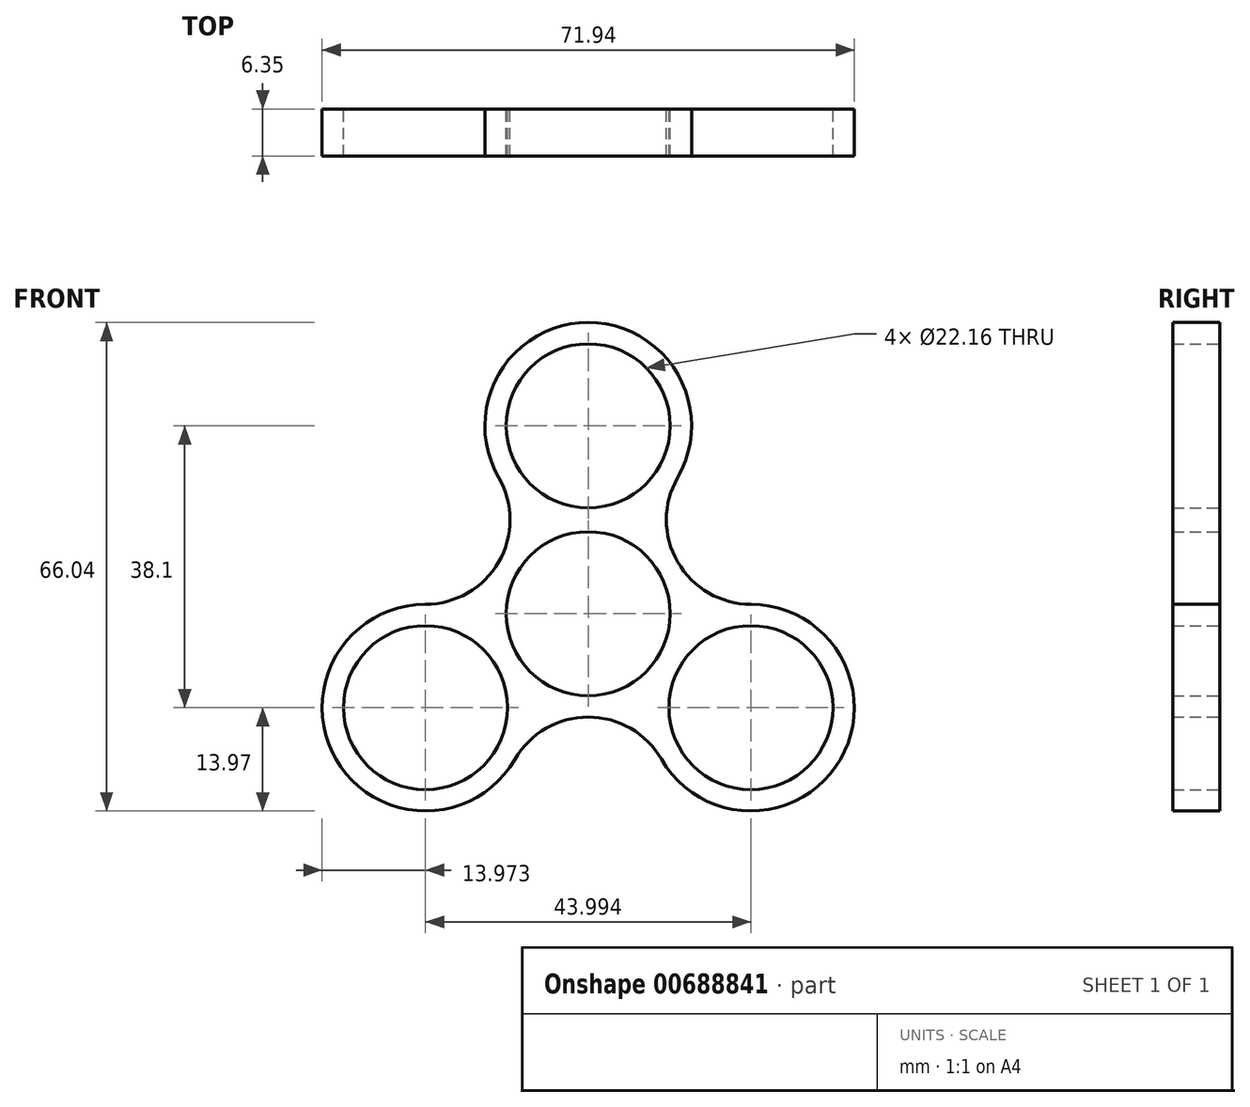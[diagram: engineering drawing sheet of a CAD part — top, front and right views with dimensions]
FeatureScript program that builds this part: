
annotation { "Feature Type Name" : "Feature", "Feature Type Description" : "" }
export const myFeature = defineFeature(function(context is Context, id is Id, definition is map)
    precondition{}
    {
        {
            var Q0;
            Q0=qCreatedBy(makeId("Front.planeOp"),FACE);
            var sketch = newSketch(context, id + "F0", { "sketchPlane" : qUnion([Q0])});
            skCircle(sketch, "E0", {"center": v(0, 0) * mm, "radius": 11.08 * mm});
            skLineSegment(sketch, "E1", {"start": v(0, 0) * mm, "end": v(0, 25.4) * mm});
            skCircle(sketch, "E2", {"center": v(0, 25.4) * mm, "radius": 11.08 * mm});
            skCircle(sketch, "E3.1.0", {"center": v(-22, -12.7) * mm, "radius": 11.08 * mm});
            skCircle(sketch, "E3.2.0", {"center": v(22, -12.7) * mm, "radius": 11.08 * mm});
            skCircle(sketch, "E4", {"center": v(0, 0) * mm, "radius": 13.97 * mm});
            skCircle(sketch, "E5", {"center": v(0, 25.4) * mm, "radius": 13.97 * mm});
            skCircle(sketch, "E6.1.0", {"center": v(-22, -12.7) * mm, "radius": 13.97 * mm});
            skCircle(sketch, "E6.2.0", {"center": v(22, -12.7) * mm, "radius": 13.97 * mm});
            skLineSegment(sketch, "E7", {"start": v(0, 0) * mm, "end": v(0, -25.4) * mm});
            skArc(sketch, "E8", {"start": v(9.9, -19.69) * mm, "mid": v(0, -13.97) * mm, "end": v(-9.9, -19.69) * mm});
            skArc(sketch, "E9.1.0", {"start": v(12.1, 18.41) * mm, "mid": v(12.1, 6.99) * mm, "end": v(22, 1.27) * mm});
            skArc(sketch, "E9.2.0", {"start": v(-22, 1.27) * mm, "mid": v(-12.1, 6.99) * mm, "end": v(-12.1, 18.42) * mm});
            skSolve(sketch);
        }
        {
            var Q0;
            {var subQ6=sQuery(id+"F0.wireOp",EDGE,"E1");var subQ7=sQuery(id+"F0.wireOp",EDGE,"E0");var subQ8=makeQuery(id+"F0.imprint","INTERSECT",VERTEX,{"derivedFrom":[subQ7,subQ6]});Q0=makeQuery(id+"F0.imprint","IMPRINT",FACE,{"disambiguationData":[TD([[makeQuery(id+"F0.imprint","IMPRINT",EDGE,{"disambiguationData":[TD([[subQ8,-1.0]])],"derivedFrom":subQ7}),-1.0]])]});}
            var Q1;
            {var subQ0=sQuery(id+"F0.wireOp",EDGE,"E6.1.0");var subQ1=sQuery(id+"F0.wireOp",EDGE,"E4");var subQ2=makeQuery(id+"F0.imprint","INTERSECT",VERTEX,{"disambiguationData":[OD(0.0)],"derivedFrom":[subQ1,subQ0]});Q1=makeQuery(id+"F0.imprint","IMPRINT",FACE,{"disambiguationData":[TD([[makeQuery(id+"F0.imprint","IMPRINT",EDGE,{"disambiguationData":[TD([[subQ2,-1.0]])],"derivedFrom":subQ1}),1.0]])]});}
            var Q2;
            Q2=makeQuery(id+"F0.imprint","IMPRINT",FACE,{"disambiguationData":[TD([[makeQuery(id+"F0.imprint","IMPRINT",EDGE,{"derivedFrom":sQuery(id+"F0.wireOp",EDGE,"E3.1.0")}),-1.0]])]});
            var Q3;
            {var subQ0=sQuery(id+"F0.wireOp",EDGE,"E9.2.0");var subQ1=sQuery(id+"F0.wireOp",EDGE,"E4");var subQ2=makeQuery(id+"F0.imprint","INTERSECT",VERTEX,{"derivedFrom":[subQ1,subQ0]});Q3=makeQuery(id+"F0.imprint","IMPRINT",FACE,{"disambiguationData":[TD([[makeQuery(id+"F0.imprint","IMPRINT",EDGE,{"disambiguationData":[TD([[subQ2,-1.0]])],"derivedFrom":subQ1}),-1.0]])]});}
            var Q4;
            {var subQ0=sQuery(id+"F0.wireOp",EDGE,"E9.2.0");var subQ1=sQuery(id+"F0.wireOp",EDGE,"E4");var subQ2=makeQuery(id+"F0.imprint","INTERSECT",VERTEX,{"derivedFrom":[subQ1,subQ0]});Q4=makeQuery(id+"F0.imprint","IMPRINT",FACE,{"disambiguationData":[TD([[makeQuery(id+"F0.imprint","IMPRINT",EDGE,{"disambiguationData":[TD([[subQ2,1.0]])],"derivedFrom":subQ1}),-1.0]])]});}
            var Q5;
            Q5=makeQuery(id+"F0.imprint","IMPRINT",FACE,{"disambiguationData":[TD([[makeQuery(id+"F0.imprint","IMPRINT",EDGE,{"derivedFrom":sQuery(id+"F0.wireOp",EDGE,"E2")}),-1.0]])]});
            var Q6;
            {var subQ0=sQuery(id+"F0.wireOp",EDGE,"E4");var subQ1=sQuery(id+"F0.wireOp",EDGE,"E1");var subQ2=makeQuery(id+"F0.imprint","INTERSECT",VERTEX,{"derivedFrom":[subQ1,subQ0]});Q6=makeQuery(id+"F0.imprint","IMPRINT",FACE,{"disambiguationData":[TD([[makeQuery(id+"F0.imprint","IMPRINT",EDGE,{"disambiguationData":[TD([[subQ2,1.0]])],"derivedFrom":subQ1}),1.0]])]});}
            var Q7;
            {var subQ0=sQuery(id+"F0.wireOp",EDGE,"E4");var subQ1=sQuery(id+"F0.wireOp",EDGE,"E1");var subQ2=makeQuery(id+"F0.imprint","INTERSECT",VERTEX,{"derivedFrom":[subQ1,subQ0]});Q7=makeQuery(id+"F0.imprint","IMPRINT",FACE,{"disambiguationData":[TD([[makeQuery(id+"F0.imprint","IMPRINT",EDGE,{"disambiguationData":[TD([[subQ2,1.0]])],"derivedFrom":subQ1}),-1.0]])]});}
            var Q8;
            {var subQ8=sQuery(id+"F0.wireOp",EDGE,"E1");var subQ9=sQuery(id+"F0.wireOp",EDGE,"E0");var subQ10=makeQuery(id+"F0.imprint","INTERSECT",VERTEX,{"derivedFrom":[subQ9,subQ8]});Q8=makeQuery(id+"F0.imprint","IMPRINT",FACE,{"disambiguationData":[TD([[makeQuery(id+"F0.imprint","IMPRINT",EDGE,{"disambiguationData":[TD([[subQ10,1.0]])],"derivedFrom":subQ9}),-1.0]])]});}
            var Q9;
            {var subQ0=sQuery(id+"F0.wireOp",EDGE,"E9.1.0");var subQ1=sQuery(id+"F0.wireOp",EDGE,"E4");var subQ2=makeQuery(id+"F0.imprint","INTERSECT",VERTEX,{"derivedFrom":[subQ1,subQ0]});Q9=makeQuery(id+"F0.imprint","IMPRINT",FACE,{"disambiguationData":[TD([[makeQuery(id+"F0.imprint","IMPRINT",EDGE,{"disambiguationData":[TD([[subQ2,-1.0]])],"derivedFrom":subQ1}),-1.0]])]});}
            var Q10;
            {var subQ0=sQuery(id+"F0.wireOp",EDGE,"E9.1.0");var subQ1=sQuery(id+"F0.wireOp",EDGE,"E4");var subQ2=makeQuery(id+"F0.imprint","INTERSECT",VERTEX,{"derivedFrom":[subQ1,subQ0]});Q10=makeQuery(id+"F0.imprint","IMPRINT",FACE,{"disambiguationData":[TD([[makeQuery(id+"F0.imprint","IMPRINT",EDGE,{"disambiguationData":[TD([[subQ2,1.0]])],"derivedFrom":subQ1}),-1.0]])]});}
            var Q11;
            Q11=makeQuery(id+"F0.imprint","IMPRINT",FACE,{"disambiguationData":[TD([[makeQuery(id+"F0.imprint","IMPRINT",EDGE,{"derivedFrom":sQuery(id+"F0.wireOp",EDGE,"E3.2.0")}),-1.0]])]});
            var Q12;
            {var subQ0=sQuery(id+"F0.wireOp",EDGE,"E6.2.0");var subQ1=sQuery(id+"F0.wireOp",EDGE,"E4");var subQ2=makeQuery(id+"F0.imprint","INTERSECT",VERTEX,{"disambiguationData":[OD(0.0)],"derivedFrom":[subQ1,subQ0]});Q12=makeQuery(id+"F0.imprint","IMPRINT",FACE,{"disambiguationData":[TD([[makeQuery(id+"F0.imprint","IMPRINT",EDGE,{"disambiguationData":[TD([[subQ2,-1.0]])],"derivedFrom":subQ1}),1.0]])]});}
            var Q13;
            {var subQ0=sQuery(id+"F0.wireOp",EDGE,"E6.1.0");var subQ3=sQuery(id+"F0.wireOp",EDGE,"E8");var subQ5=makeQuery(id+"F0.imprint","INTERSECT",VERTEX,{"derivedFrom":[subQ0,subQ3]});Q13=makeQuery(id+"F0.imprint","IMPRINT",FACE,{"disambiguationData":[TD([[makeQuery(id+"F0.imprint","IMPRINT",EDGE,{"disambiguationData":[TD([[subQ5,-1.0]])],"derivedFrom":subQ0}),-1.0]])]});}
            var Q14;
            {var subQ0=sQuery(id+"F0.wireOp",EDGE,"E8");var subQ3=sQuery(id+"F0.wireOp",EDGE,"E6.2.0");var subQ5=makeQuery(id+"F0.imprint","INTERSECT",VERTEX,{"derivedFrom":[subQ3,subQ0]});Q14=makeQuery(id+"F0.imprint","IMPRINT",FACE,{"disambiguationData":[TD([[makeQuery(id+"F0.imprint","IMPRINT",EDGE,{"disambiguationData":[TD([[subQ5,1.0]])],"derivedFrom":subQ3}),-1.0]])]});}
            extrude(context, id + "F1", {"entities" : qUnion([Q0, Q1, Q2, Q3, Q4, Q5, Q6, Q7, Q8, Q9, Q10, Q11, Q12, Q13, Q14]), "depth" : 6.35 * mm, "offsetDistance" : 25.4 * mm});
        }
    });
